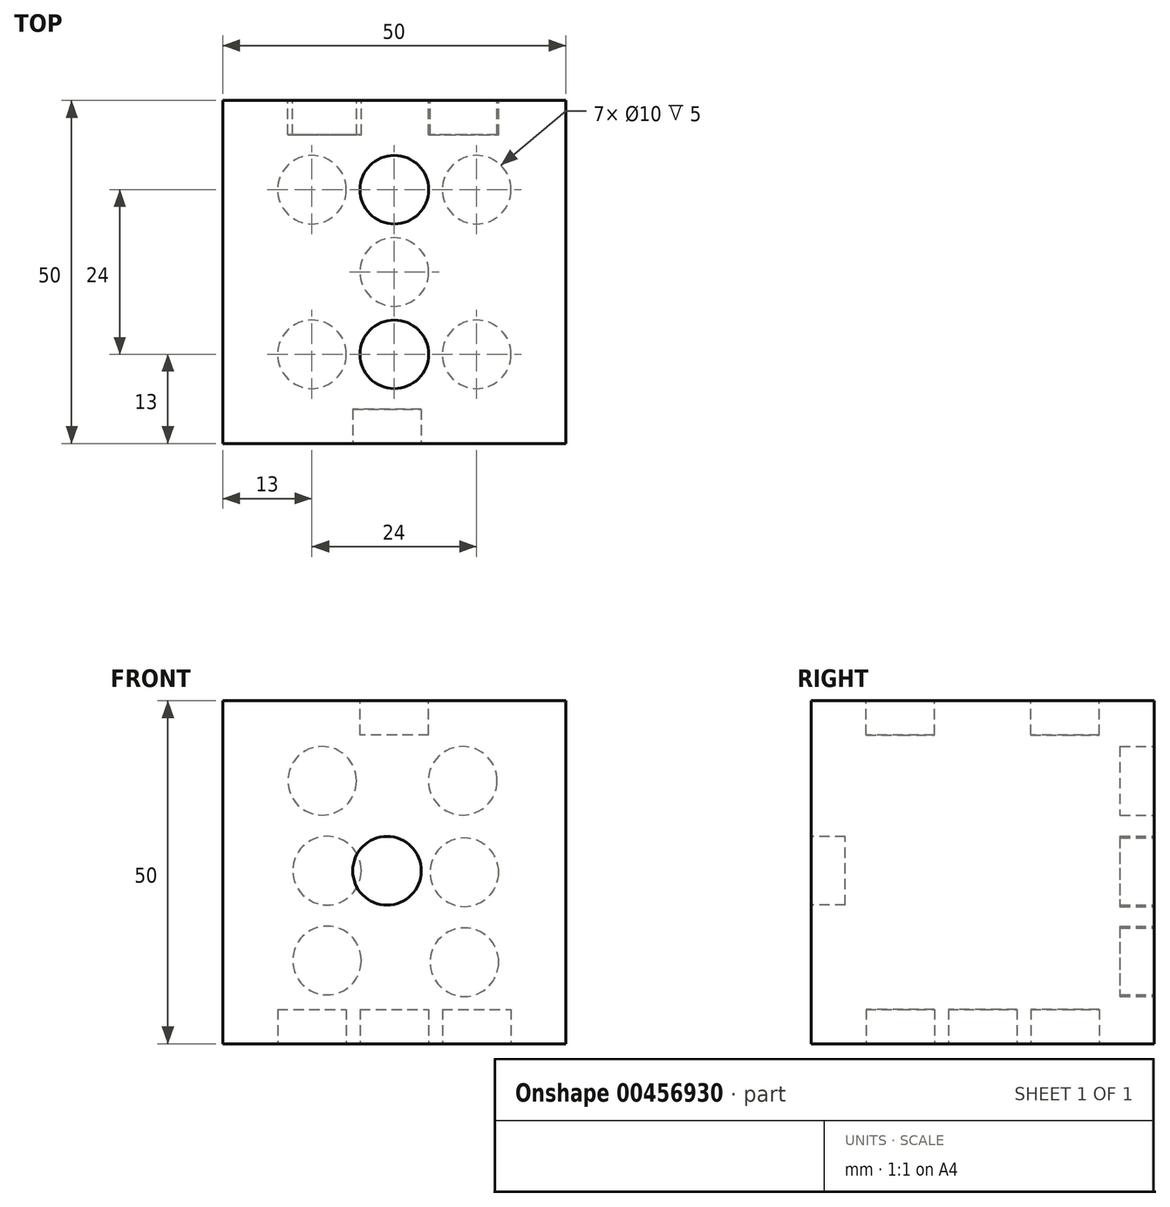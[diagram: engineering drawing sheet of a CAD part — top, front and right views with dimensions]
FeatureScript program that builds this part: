
annotation { "Feature Type Name" : "Feature", "Feature Type Description" : "" }
export const myFeature = defineFeature(function(context is Context, id is Id, definition is map)
    precondition{}
    {
        {
            var Q0;
            Q0=qCreatedBy(makeId("Front.planeOp"),FACE);
            var sketch = newSketch(context, id + "F0", { "sketchPlane" : qUnion([Q0])});
            skLineSegment(sketch, "E0.bottom", {"start": v(0, 0) * mm, "end": v(-50, 0) * mm});
            skLineSegment(sketch, "E0.top", {"start": v(0, 50) * mm, "end": v(-50, 50) * mm});
            skLineSegment(sketch, "E0.left", {"start": v(0, 0) * mm, "end": v(0, 50) * mm});
            skLineSegment(sketch, "E0.right", {"start": v(-50, 0) * mm, "end": v(-50, 50) * mm});
            skSolve(sketch);
        }
        {
            var Q0;
            Q0=qCreatedBy(makeId("Front.planeOp"),FACE);
            cPlane(context, id + "F1", {"entities" : qUnion([Q0]), "cplaneType" : CPlaneType.OFFSET, "offset" : 50 * mm, "width" : 150 * mm, "height" : 150 * mm});
        }
        {
            var Q0;
            Q0=qCreatedBy(id+"F1.planeOp",FACE);
            var sketch = newSketch(context, id + "F2", { "sketchPlane" : qUnion([Q0])});
            skLineSegment(sketch, "E1.bottom", {"start": v(0, 0) * mm, "end": v(-50, 0) * mm});
            skLineSegment(sketch, "E1.top", {"start": v(0, 50) * mm, "end": v(-50, 50) * mm});
            skLineSegment(sketch, "E1.left", {"start": v(0, 0) * mm, "end": v(0, 50) * mm});
            skLineSegment(sketch, "E1.right", {"start": v(-50, 0) * mm, "end": v(-50, 50) * mm});
            skSolve(sketch);
        }
        {
            var Q0;
            Q0=makeQuery(id+"F0.imprint","IMPRINT",FACE,{"disambiguationData":[TD([[makeQuery(id+"F0.imprint","IMPRINT",EDGE,{"derivedFrom":sQuery(id+"F0.wireOp",EDGE,"E0.bottom")}),-1.0]])]});
            var Q1;
            Q1=makeQuery(id+"F2.imprint","IMPRINT",FACE,{"disambiguationData":[TD([[makeQuery(id+"F2.imprint","IMPRINT",EDGE,{"derivedFrom":sQuery(id+"F2.wireOp",EDGE,"E1.bottom")}),-1.0]])]});
            loft(context, id + "F3", {"sheetProfilesArray" : [{ "sheetProfileEntities" : qUnion([Q0]) }, { "sheetProfileEntities" : qUnion([Q1]) }]});
        }
        {
            var Q0;
            Q0=makeQuery(id+"F3.opLoft","CAP_FACE",FACE,{"disambiguationData":[OSD([makeQuery(id+"F2.imprint","IMPRINT",FACE,{"disambiguationData":[TD([[makeQuery(id+"F2.imprint","IMPRINT",EDGE,{"derivedFrom":sQuery(id+"F2.wireOp",EDGE,"E1.bottom")}),-1.0]])]})])],"isStart":true});
            var sketch = newSketch(context, id + "F4", { "sketchPlane" : qUnion([Q0])});
            skCircle(sketch, "E2", {"center": v(-26.06, 25.21) * mm, "radius": 5 * mm});
            skSolve(sketch);
        }
        {
            var Q0;
            Q0=makeQuery(id+"F4.imprint","IMPRINT",FACE,{"disambiguationData":[TD([[makeQuery(id+"F4.imprint","IMPRINT",EDGE,{"derivedFrom":sQuery(id+"F4.wireOp",EDGE,"E2")}),1.0]])]});
            extrude(context, id + "F5", {"entities" : qUnion([Q0]), "operationType" : NewBodyOperationType.REMOVE, "oppositeDirection" : true, "depth" : 5 * mm});
        }
        {
            var Q0;
            Q0=makeQuery(id+"F3.opLoft","SWEPT_FACE",FACE,{"disambiguationData":[OSD([sQuery(id+"F0.wireOp",EDGE,"E0.bottom"),sQuery(id+"F0.wireOp",EDGE,"E0.left"),sQuery(id+"F0.wireOp",EDGE,"E0.right"),sQuery(id+"F2.wireOp",EDGE,"E1.bottom"),sQuery(id+"F2.wireOp",EDGE,"E1.left"),sQuery(id+"F2.wireOp",EDGE,"E1.right")])]});
            var sketch = newSketch(context, id + "F6", { "sketchPlane" : qUnion([Q0])});
            skLineSegment(sketch, "E3", {"start": v(-50, 50) * mm, "end": v(0, 0) * mm, "construction": true});
            skLineSegment(sketch, "E4", {"start": v(0, 50) * mm, "end": v(-50, 0) * mm, "construction": true});
            skCircle(sketch, "E5", {"center": v(-25, 25) * mm, "radius": 5 * mm});
            skCircle(sketch, "E6", {"center": v(-37, 37) * mm, "radius": 5 * mm});
            skCircle(sketch, "E7", {"center": v(-13, 37) * mm, "radius": 5 * mm});
            skCircle(sketch, "E8", {"center": v(-13, 13) * mm, "radius": 5 * mm});
            skCircle(sketch, "E9", {"center": v(-37, 13) * mm, "radius": 5 * mm});
            skSolve(sketch);
        }
        {
            var Q0;
            Q0 = qSketchRegion(id + "F6", true);
            extrude(context, id + "F7", {"entities" : qUnion([Q0]), "operationType" : NewBodyOperationType.REMOVE, "oppositeDirection" : true, "depth" : 5 * mm});
        }
        {
            var Q0;
            Q0=makeQuery(id+"F3.opLoft","CAP_FACE",FACE,{"disambiguationData":[OSD([makeQuery(id+"F0.imprint","IMPRINT",FACE,{"disambiguationData":[TD([[makeQuery(id+"F0.imprint","IMPRINT",EDGE,{"derivedFrom":sQuery(id+"F0.wireOp",EDGE,"E0.bottom")}),-1.0]])]})])],"isStart":true});
            var sketch = newSketch(context, id + "F8", { "sketchPlane" : qUnion([Q0])});
            skLineSegment(sketch, "E10", {"start": v(15, 50) * mm, "end": v(15, 0) * mm, "construction": true});
            skLineSegment(sketch, "E11", {"start": v(35, 50) * mm, "end": v(35, 0) * mm, "construction": true});
            skLineSegment(sketch, "E12", {"start": v(0, 38) * mm, "end": v(50, 38) * mm, "construction": true});
            skLineSegment(sketch, "E13", {"start": v(0, 25) * mm, "end": v(50, 25) * mm, "construction": true});
            skLineSegment(sketch, "E14", {"start": v(0, 12) * mm, "end": v(50, 12) * mm, "construction": true});
            skSolve(sketch);
        }
        {
            var Q0;
            {var subQ0=sQuery(id+"F0.wireOp",EDGE,"E0.right");var subQ1=sQuery(id+"F0.wireOp",EDGE,"E0.left");var subQ2=sQuery(id+"F0.wireOp",EDGE,"E0.bottom");Q0=makeQuery(id+"F8.imprint","IMPRINT",FACE,{"disambiguationData":[TD([[makeQuery(id+"F8.imprint","IMPRINT",EDGE,{"derivedFrom":makeQuery(id+"F3.opLoft","MID_CAP_EDGE",EDGE,{"disambiguationData":[OSD([subQ2,subQ1,subQ0])],"capPos":0.0})}),-1.0]])]});}
            var sketch = newSketch(context, id + "F9", { "sketchPlane" : qUnion([Q0])});
            skCircle(sketch, "E15", {"center": v(15.03, 38.34) * mm, "radius": 5 * mm});
            skCircle(sketch, "E16", {"center": v(14.79, 25) * mm, "radius": 5 * mm});
            skCircle(sketch, "E17", {"center": v(14.79, 11.9) * mm, "radius": 5 * mm});
            skCircle(sketch, "E18", {"center": v(35.51, 38.34) * mm, "radius": 5 * mm});
            skCircle(sketch, "E19", {"center": v(34.8, 25.24) * mm, "radius": 5 * mm});
            skCircle(sketch, "E20", {"center": v(34.8, 12.13) * mm, "radius": 5 * mm});
            skSolve(sketch);
        }
        {
            var Q0;
            Q0 = qSketchRegion(id + "F9", true);
            extrude(context, id + "F10", {"entities" : qUnion([Q0]), "operationType" : NewBodyOperationType.REMOVE, "oppositeDirection" : true, "depth" : 5 * mm});
        }
        {
            var Q0;
            Q0=makeQuery(id+"F3.opLoft","SWEPT_FACE",FACE,{"disambiguationData":[OSD([sQuery(id+"F0.wireOp",EDGE,"E0.top"),sQuery(id+"F0.wireOp",EDGE,"E0.left"),sQuery(id+"F0.wireOp",EDGE,"E0.right"),sQuery(id+"F2.wireOp",EDGE,"E1.top"),sQuery(id+"F2.wireOp",EDGE,"E1.left"),sQuery(id+"F2.wireOp",EDGE,"E1.right")])]});
            var sketch = newSketch(context, id + "F11", { "sketchPlane" : qUnion([Q0])});
            skLineSegment(sketch, "E21", {"start": v(-50, -13) * mm, "end": v(0, -13) * mm, "construction": true});
            skLineSegment(sketch, "E22", {"start": v(-50, -37) * mm, "end": v(0, -37) * mm, "construction": true});
            skLineSegment(sketch, "E23", {"start": v(-25, 0) * mm, "end": v(-25, -50) * mm, "construction": true});
            skCircle(sketch, "E24", {"center": v(-25, -13) * mm, "radius": 5 * mm});
            skCircle(sketch, "E25", {"center": v(-25, -37) * mm, "radius": 5 * mm});
            skSolve(sketch);
        }
        {
            var Q0;
            Q0=makeQuery(id+"F11.imprint","IMPRINT",FACE,{"disambiguationData":[TD([[makeQuery(id+"F11.imprint","IMPRINT",EDGE,{"derivedFrom":sQuery(id+"F11.wireOp",EDGE,"E25")}),1.0]])]});
            var Q1;
            Q1=makeQuery(id+"F11.imprint","IMPRINT",FACE,{"disambiguationData":[TD([[makeQuery(id+"F11.imprint","IMPRINT",EDGE,{"derivedFrom":sQuery(id+"F11.wireOp",EDGE,"E24")}),1.0]])]});
            extrude(context, id + "F12", {"entities" : qUnion([Q0, Q1]), "operationType" : NewBodyOperationType.REMOVE, "oppositeDirection" : true, "depth" : 5 * mm});
        }
    });
